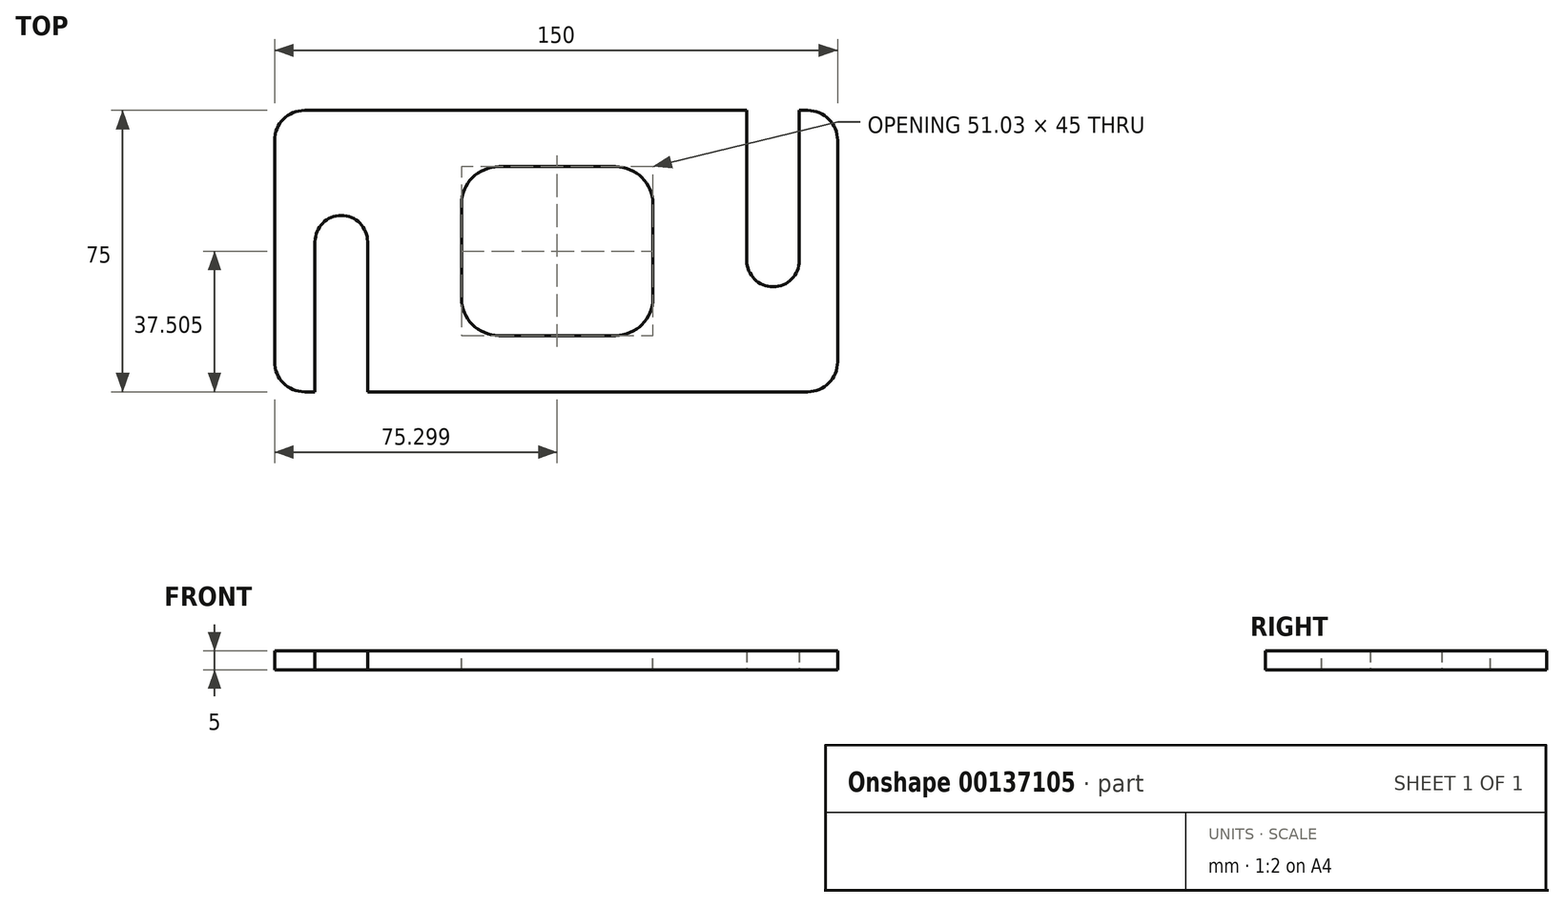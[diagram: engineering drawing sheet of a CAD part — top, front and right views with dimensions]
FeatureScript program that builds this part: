
annotation { "Feature Type Name" : "Feature", "Feature Type Description" : "" }
export const myFeature = defineFeature(function(context is Context, id is Id, definition is map)
    precondition{}
    {
        {
            var Q0;
            Q0=qCreatedBy(makeId("Top.planeOp"),FACE);
            var sketch = newSketch(context, id + "F0", { "sketchPlane" : qUnion([Q0])});
            skLineSegment(sketch, "E0.bottom", {"start": v(-108.92, -70.74) * mm, "end": v(41.08, -70.74) * mm});
            skLineSegment(sketch, "E0.top", {"start": v(-108.92, -145.74) * mm, "end": v(41.08, -145.74) * mm});
            skLineSegment(sketch, "E0.left", {"start": v(-108.92, -70.74) * mm, "end": v(-108.92, -145.74) * mm});
            skLineSegment(sketch, "E0.right", {"start": v(41.08, -70.74) * mm, "end": v(41.08, -145.74) * mm});
            skSolve(sketch);
        }
        {
            var Q0;
            Q0=makeQuery(id+"F0.imprint","IMPRINT",FACE,{"disambiguationData":[TD([[makeQuery(id+"F0.imprint","IMPRINT",EDGE,{"derivedFrom":sQuery(id+"F0.wireOp",EDGE,"E0.bottom")}),-1.0]])]});
            extrude(context, id + "F1", {"entities" : qUnion([Q0]), "depth" : 5 * mm});
        }
        {
            var Q0;
            Q0=qCreatedBy(makeId("Top.planeOp"),FACE);
            var sketch = newSketch(context, id + "F2", { "sketchPlane" : qUnion([Q0])});
            skLineSegment(sketch, "E1", {"start": v(-98.13, -145.74) * mm, "end": v(-98.13, -105.74) * mm});
            skLineSegment(sketch, "E2", {"start": v(-84.13, -145.74) * mm, "end": v(-84.13, -105.74) * mm});
            skArc(sketch, "E3", {"start": v(-98.13, -105.74) * mm, "mid": v(-91.13, -98.74) * mm, "end": v(-84.13, -105.74) * mm});
            skLineSegment(sketch, "E4", {"start": v(-98.13, -145.74) * mm, "end": v(-84.13, -145.74) * mm});
            skLineSegment(sketch, "E5", {"start": v(30.9, -70.74) * mm, "end": v(30.9, -110.74) * mm});
            skLineSegment(sketch, "E6", {"start": v(16.9, -70.74) * mm, "end": v(16.9, -110.74) * mm});
            skLineSegment(sketch, "E7", {"start": v(16.9, -70.74) * mm, "end": v(30.9, -70.74) * mm});
            skArc(sketch, "E8", {"start": v(16.9, -110.74) * mm, "mid": v(23.9, -117.74) * mm, "end": v(30.9, -110.74) * mm});
            skSolve(sketch);
        }
        {
            var Q0;
            Q0 = qSketchRegion(id + "F2", true);
            extrude(context, id + "F3", {"entities" : qUnion([Q0]), "operationType" : NewBodyOperationType.REMOVE, "endBound" : BoundingType.THROUGH_ALL, "oppositeDirection" : true, "depth" : 25.4 * mm});
        }
        {
            var Q0;
            Q0 = qSketchRegion(id + "F2", true);
            extrude(context, id + "F4", {"entities" : qUnion([Q0]), "operationType" : NewBodyOperationType.REMOVE, "endBound" : BoundingType.THROUGH_ALL, "depth" : 25.4 * mm});
        }
        {
            var Q0;
            Q0=makeQuery(id+"F1.opExtrude","CAP_FACE",FACE,{"disambiguationData":[OSD([sQuery(id+"F0.wireOp",EDGE,"E0.bottom"),sQuery(id+"F0.wireOp",EDGE,"E0.top"),sQuery(id+"F0.wireOp",EDGE,"E0.left"),sQuery(id+"F0.wireOp",EDGE,"E0.right")])],"isStart":false});
            var sketch = newSketch(context, id + "F5", { "sketchPlane" : qUnion([Q0])});
            skLineSegment(sketch, "E9.bottom", {"start": v(-59.13, -130.74) * mm, "end": v(-8.1, -130.74) * mm});
            skLineSegment(sketch, "E9.top", {"start": v(-59.13, -85.74) * mm, "end": v(-8.1, -85.74) * mm});
            skLineSegment(sketch, "E9.left", {"start": v(-59.13, -130.74) * mm, "end": v(-59.13, -85.74) * mm});
            skLineSegment(sketch, "E9.right", {"start": v(-8.1, -130.74) * mm, "end": v(-8.1, -85.74) * mm});
            skSolve(sketch);
        }
        {
            var Q0;
            Q0=makeQuery(id+"F5.imprint","IMPRINT",FACE,{"disambiguationData":[TD([[makeQuery(id+"F5.imprint","IMPRINT",EDGE,{"derivedFrom":sQuery(id+"F5.wireOp",EDGE,"E9.bottom")}),1.0]])]});
            extrude(context, id + "F6", {"entities" : qUnion([Q0]), "operationType" : NewBodyOperationType.REMOVE, "endBound" : BoundingType.THROUGH_ALL, "oppositeDirection" : true, "depth" : 25.4 * mm});
        }
        {
            var Q0;
            Q0=makeQuery(id+"F6.boolean.opBoolean","COPY",EDGE,{"derivedFrom":makeQuery(id+"F6.opExtrude","SWEPT_EDGE",EDGE,{"disambiguationData":[OSD([sQuery(id+"F5.wireOp",EDGE,"E9.top"),sQuery(id+"F5.wireOp",EDGE,"E9.right")])]})});
            var Q1;
            Q1=makeQuery(id+"F6.boolean.opBoolean","COPY",EDGE,{"derivedFrom":makeQuery(id+"F6.opExtrude","SWEPT_EDGE",EDGE,{"disambiguationData":[OSD([sQuery(id+"F5.wireOp",EDGE,"E9.bottom"),sQuery(id+"F5.wireOp",EDGE,"E9.right")])]})});
            var Q2;
            Q2=makeQuery(id+"F6.boolean.opBoolean","COPY",EDGE,{"derivedFrom":makeQuery(id+"F6.opExtrude","SWEPT_EDGE",EDGE,{"disambiguationData":[OSD([sQuery(id+"F5.wireOp",EDGE,"E9.bottom"),sQuery(id+"F5.wireOp",EDGE,"E9.left")])]})});
            var Q3;
            Q3=makeQuery(id+"F6.boolean.opBoolean","COPY",EDGE,{"derivedFrom":makeQuery(id+"F6.opExtrude","SWEPT_EDGE",EDGE,{"disambiguationData":[OSD([sQuery(id+"F5.wireOp",EDGE,"E9.top"),sQuery(id+"F5.wireOp",EDGE,"E9.left")])]})});
            fillet(context, id + "F7", {"entities" : qUnion([Q0, Q1, Q2, Q3]), "radius" : 10 * mm, "tangentPropagation" : true, "allowEdgeOverflow" : false});
        }
        {
            var Q0;
            Q0=makeQuery(id+"F1.opExtrude","SWEPT_EDGE",EDGE,{"disambiguationData":[OSD([sQuery(id+"F0.wireOp",EDGE,"E0.top"),sQuery(id+"F0.wireOp",EDGE,"E0.right")])]});
            var Q1;
            Q1=makeQuery(id+"F1.opExtrude","SWEPT_EDGE",EDGE,{"disambiguationData":[OSD([sQuery(id+"F0.wireOp",EDGE,"E0.bottom"),sQuery(id+"F0.wireOp",EDGE,"E0.right")])]});
            var Q2;
            Q2=makeQuery(id+"F1.opExtrude","SWEPT_EDGE",EDGE,{"disambiguationData":[OSD([sQuery(id+"F0.wireOp",EDGE,"E0.bottom"),sQuery(id+"F0.wireOp",EDGE,"E0.left")])]});
            var Q3;
            Q3=makeQuery(id+"F1.opExtrude","SWEPT_EDGE",EDGE,{"disambiguationData":[OSD([sQuery(id+"F0.wireOp",EDGE,"E0.top"),sQuery(id+"F0.wireOp",EDGE,"E0.left")])]});
            fillet(context, id + "F8", {"entities" : qUnion([Q0, Q1, Q2, Q3]), "radius" : 8 * mm, "tangentPropagation" : true, "allowEdgeOverflow" : false});
        }
    });
